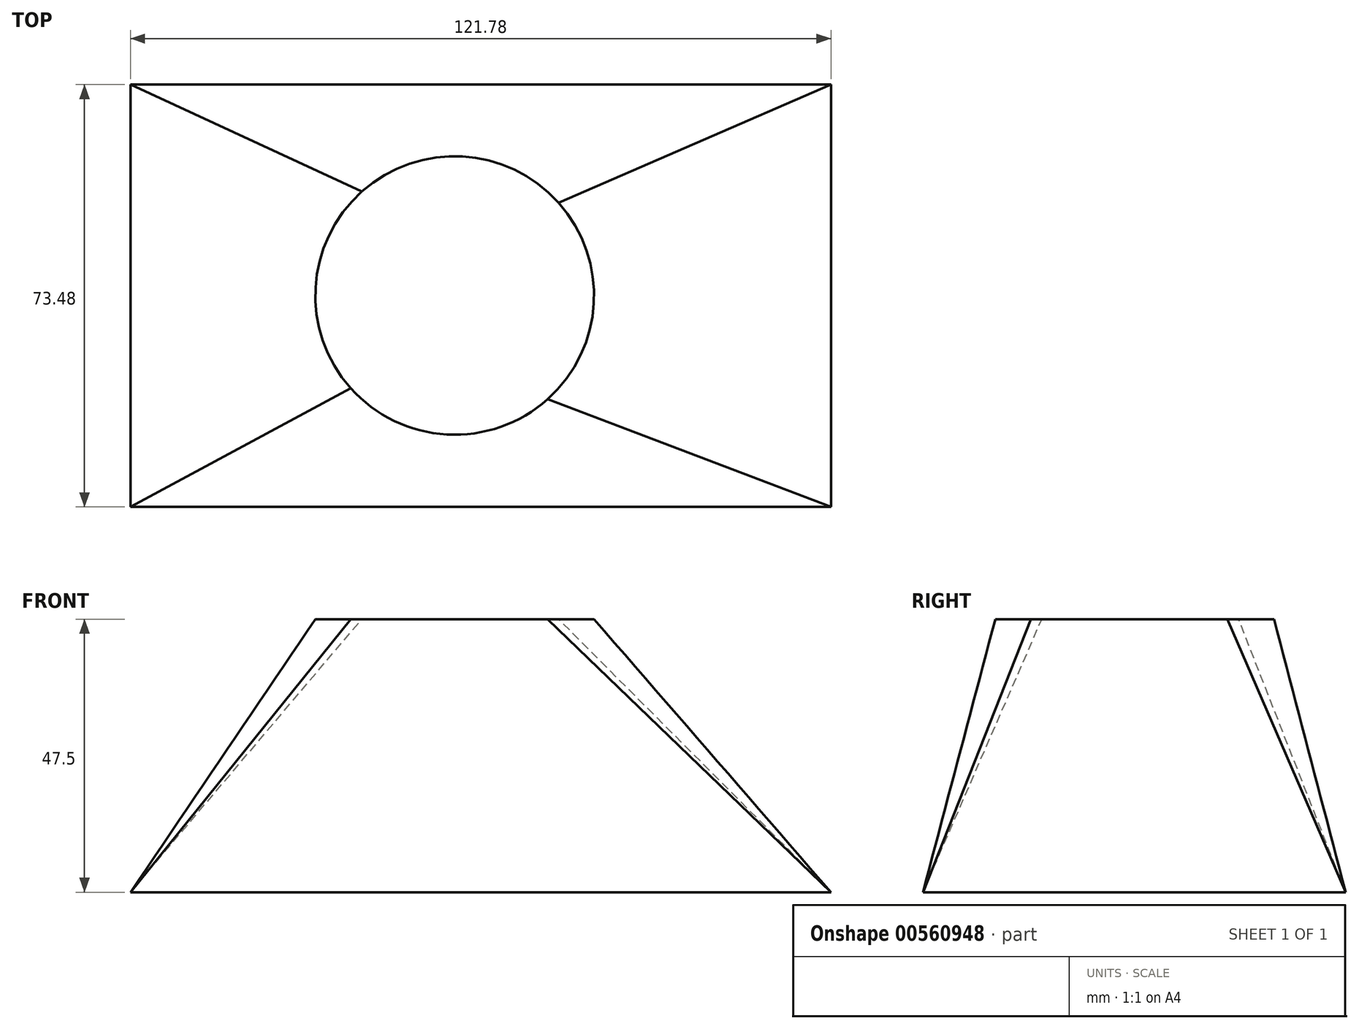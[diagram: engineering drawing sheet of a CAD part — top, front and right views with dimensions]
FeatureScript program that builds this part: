
annotation { "Feature Type Name" : "Feature", "Feature Type Description" : "" }
export const myFeature = defineFeature(function(context is Context, id is Id, definition is map)
    precondition{}
    {
        {
            var Q0;
            Q0=qCreatedBy(makeId("Top.planeOp"),FACE);
            cPlane(context, id + "F0", {"entities" : qUnion([Q0]), "cplaneType" : CPlaneType.OFFSET, "offset" : 47.5 * mm, "width" : 152.4 * mm, "height" : 152.4 * mm});
        }
        {
            var Q0;
            Q0=qCreatedBy(makeId("Top.planeOp"),FACE);
            var sketch = newSketch(context, id + "F1", { "sketchPlane" : qUnion([Q0])});
            skLineSegment(sketch, "E0.bottom", {"start": v(-88.7, 58.97) * mm, "end": v(33.08, 58.97) * mm});
            skLineSegment(sketch, "E0.top", {"start": v(-88.7, -14.5) * mm, "end": v(33.08, -14.5) * mm});
            skLineSegment(sketch, "E0.left", {"start": v(-88.7, 58.97) * mm, "end": v(-88.7, -14.5) * mm});
            skLineSegment(sketch, "E0.right", {"start": v(33.08, 58.97) * mm, "end": v(33.08, -14.5) * mm});
            skSolve(sketch);
        }
        {
            var Q0;
            Q0=qCreatedBy(id+"F0.planeOp",FACE);
            var sketch = newSketch(context, id + "F2", { "sketchPlane" : qUnion([Q0])});
            skCircle(sketch, "E1", {"center": v(-32.33, 22.3) * mm, "radius": 24.22 * mm});
            skLineSegment(sketch, "E2", {"start": v(-32.53, 46.52) * mm, "end": v(-32.53, -1.93) * mm, "construction": true});
            skPoint(sketch, "E3", {"position": v(-49.16, 39.72) * mm});
            skPoint(sketch, "E4", {"position": v(-50.4, 6.16) * mm});
            skPoint(sketch, "E5", {"position": v(-13.42, 6.47) * mm});
            skPoint(sketch, "E6", {"position": v(-16.2, 40.36) * mm});
            skSolve(sketch);
        }
        {
            var Q0;
            Q0 = qSketchRegion(id + "F1", true);
            var Q1;
            Q1 = qSketchRegion(id + "F2", true);
            var Q2;
            Q2=sQuery(id+"F1.wireOp",VERTEX,"E0.top.end");
            var Q3;
            Q3=sQuery(id+"F2.wireOp",VERTEX,"E4");
            var Q4;
            Q4=sQuery(id+"F1.wireOp",VERTEX,"E0.left.end");
            loft(context, id + "F3", {"sheetProfilesArray" : [{ "sheetProfileEntities" : qUnion([Q0]) }, { "sheetProfileEntities" : qUnion([Q1]) }], "wireProfilesArray" : [{ "wireProfileEntities" : qUnion([Q2]) }], "matchConnections" : true, "connections" : [{ "connectionEntities" : qUnion([Q3, Q4]), "connectionEdgeQueries" : qUnion([]), "connectionEdgeParameters" : [] }]});
        }
    });
